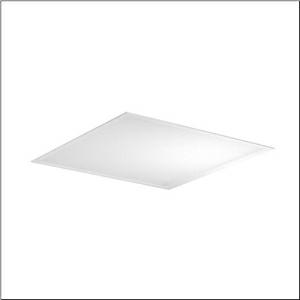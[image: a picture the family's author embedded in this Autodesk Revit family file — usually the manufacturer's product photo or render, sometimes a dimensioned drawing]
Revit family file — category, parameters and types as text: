
# Revit family: apollon_21_square_51mq12wd2454
name_source: partatom
category: Lighting Fixtures
units: mm (PartAtom-declared; Revit-internal decimal feet)

## family parameters
Cut with Voids When Loaded = No
Host = Face
Light Source = No
Part Type = Normal
Room Calculation Point = No
Round Connector Dimension = Use Diameter
Shared = No

## types (1)
- Apollon 21 square (1 x LED, 4200 lm, 24.7 W, 4000K)
    Apparent Load = 25 VA
    CIE Flux Codes = 60 87 97 100 100
    Color Rendering = 80
    Color Temperature = 4000K
    Default Elevation = 1800 mm
    Description = Apollon 21 square, office luminaire, primary optical cover: micro prismatic cover, of PMMA, CAT 2 (L<= 3000cd/m²), light emission: direct distribution, primary light characteristic: symmetric, installation type: lay-in mounting, LED, rated luminous flux: 4.200lm, luminous efficacy: 170lm/W, light colour: 840, colour temperature: 4000K, control gear: DALI 2, Multilumen, with terminal, 5-pole, mains connection: 220..240V, AC/DC, 0/50..60Hz, rated input power: 24.7W, housing, of aluminium, coated, traffic white (RAL 9016), module: M600, length: 595mm, width: 595mm, height: 55mm, recess depth: 180mm, housing upper side, of sheet steel, galvanised, protection rating (complete): IP20, protection rating (lamp compartment, on room side): IP54, insulation class (complete): insulation class II (safety insulation), certification: CE, ENEC, impact resistance: IK03, permissible operating ambient temperature: -20..+45°C, permissible storage temperature: -40..+80°C, standard: EN 60598-2-22, packaging unit: 1 piece
    Height = 0 mm  [stored 0 ft]
    Lamp = 1 x LED
    Lamp Light Flux = 4200 lm
    Lamp Power = 24.7 W
    Lamp count = 1
    Length = 595 mm
    Luminous efficacy = 170 lm/W
    Manufacturer = Siteco
    ModVariant = No
    Model = 51MQ12WD2454
    Mounting Place = Ceiling
    Mounting Type = Recessed
    Number of Poles = 1
    OnlyDefault = Yes
    Power Factor = 1
    Product Name = Apollon 21 square
    Product group = office luminaire | ceiling recessed
    ProductGroupID = 401
    Protection Class = Protection class II
    Protection Degree = IP 20
    RLX_Detail_Level = 1
    RLX_Emergency_Light_Flux = 0 lm
    RLX_Emergency_Type = 0
    RLX_Emergency_Type_DB = No
    RlxData = <blob elided: 12561 chars, md5=3fef94b0>
    Socket = socket
    Standby Power = 0 W
    System Light Flux = 4200 lm
    System Power = 25 W
    Type Comments = Product without accessories
    Type Image = l_1291049.jpg
    URL = http://relux.com
    VarID = ---
    Voltage = 0 V
    Weight = 0.00 kg
    Width = 595 mm

note: [stored X ft] marks values corroborated as IEEE doubles in the binary element streams (Revit-internal decimal feet)

## geometry (parser evidence)
native form markers: Sweep x12
no freeform markers — native parametric forms only
